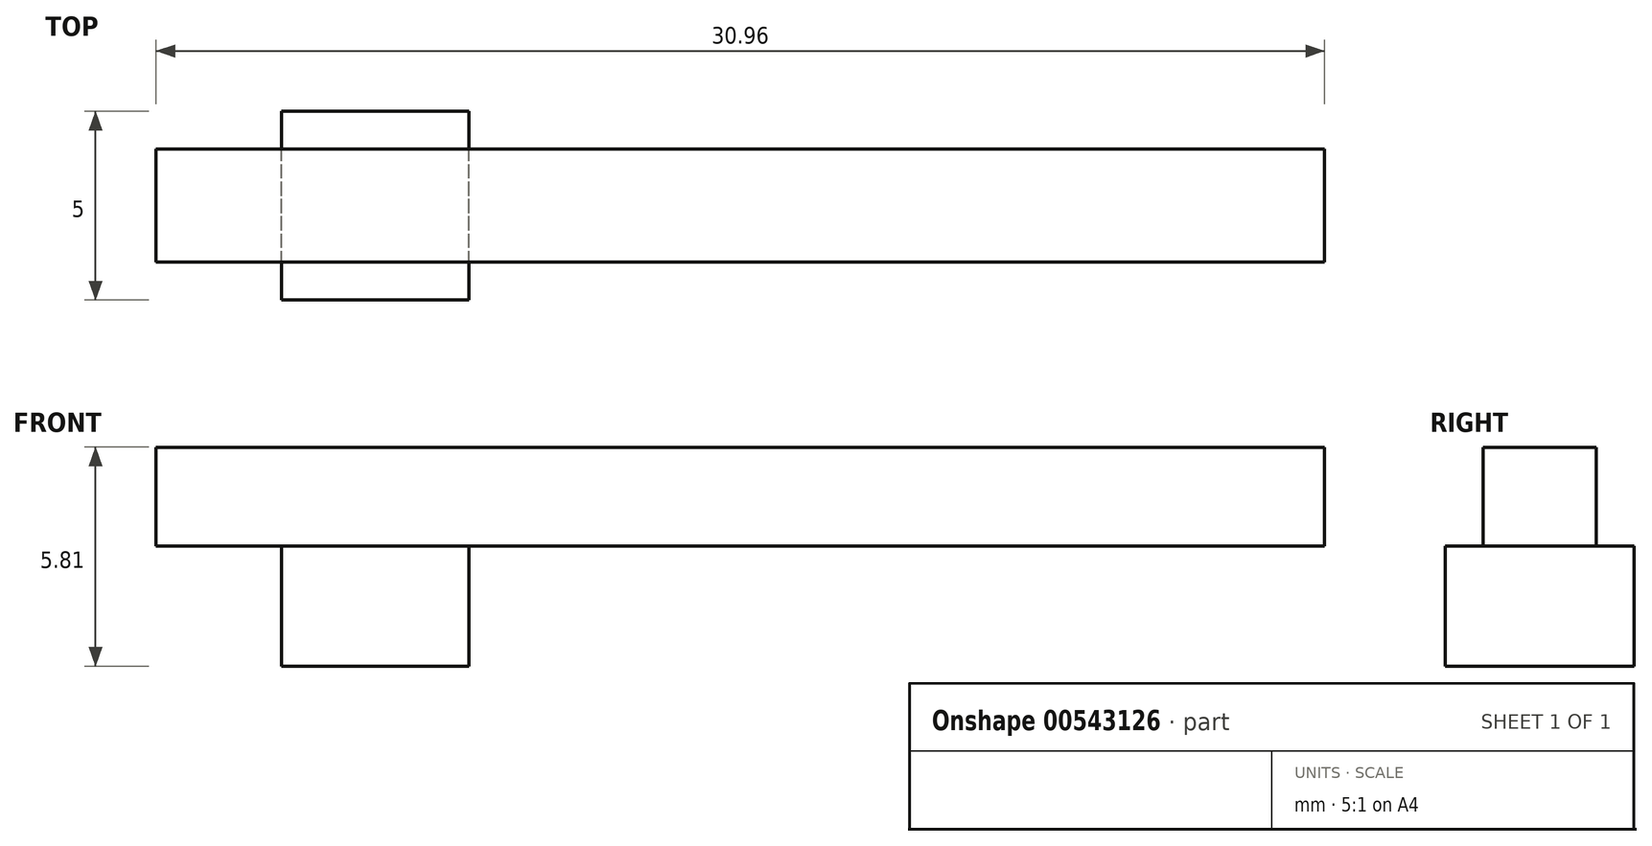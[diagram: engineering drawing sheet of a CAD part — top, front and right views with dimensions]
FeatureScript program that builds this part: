
annotation { "Feature Type Name" : "Feature", "Feature Type Description" : "" }
export const myFeature = defineFeature(function(context is Context, id is Id, definition is map)
    precondition{}
    {
        {
            var Q0;
            Q0=qCreatedBy(makeId("Front.planeOp"),FACE);
            var sketch = newSketch(context, id + "F0", { "sketchPlane" : qUnion([Q0])});
            skLineSegment(sketch, "E0", {"start": v(-43.67, 0) * mm, "end": v(-48.92, 0) * mm});
            skLineSegment(sketch, "E1", {"start": v(-48.92, 0) * mm, "end": v(-48.92, 2.63) * mm});
            skLineSegment(sketch, "E2", {"start": v(-48.92, 2.63) * mm, "end": v(-17.96, 2.63) * mm});
            skLineSegment(sketch, "E3", {"start": v(-17.96, 2.63) * mm, "end": v(-17.96, 0) * mm});
            skLineSegment(sketch, "E4", {"start": v(-17.96, 0) * mm, "end": v(-48.92, 0) * mm});
            skSolve(sketch);
        }
        {
            var Q0;
            {var subQ0=sQuery(id+"F0.wireOp",EDGE,"E1");Q0=makeQuery(id+"F0.imprint","IMPRINT",FACE,{"disambiguationData":[TD([[makeQuery(id+"F0.imprint","IMPRINT",EDGE,{"derivedFrom":subQ0}),-1.0]])]});}
            extrude(context, id + "F1", {"entities" : qUnion([Q0]), "endBound" : BoundingType.SYMMETRIC, "depth" : 3 * mm, "offsetDistance" : 25.4 * mm});
        }
        {
            var Q0;
            Q0=qCreatedBy(makeId("Front.planeOp"),FACE);
            var sketch = newSketch(context, id + "F2", { "sketchPlane" : qUnion([Q0])});
            skLineSegment(sketch, "E5", {"start": v(-45.6, 0) * mm, "end": v(-45.6, -3.18) * mm});
            skLineSegment(sketch, "E6", {"start": v(-45.6, -3.18) * mm, "end": v(-40.63, -3.18) * mm});
            skLineSegment(sketch, "E7", {"start": v(-40.63, -3.18) * mm, "end": v(-40.63, 0) * mm});
            skLineSegment(sketch, "E8", {"start": v(-45.6, 0) * mm, "end": v(-40.63, 0) * mm});
            skSolve(sketch);
        }
        {
            var Q0;
            Q0=makeQuery(id+"F2.imprint","IMPRINT",FACE,{"disambiguationData":[TD([[makeQuery(id+"F2.imprint","IMPRINT",EDGE,{"derivedFrom":sQuery(id+"F2.wireOp",EDGE,"E5")}),1.0]])]});
            extrude(context, id + "F3", {"entities" : qUnion([Q0]), "operationType" : NewBodyOperationType.ADD, "endBound" : BoundingType.SYMMETRIC, "depth" : 5 * mm, "offsetDistance" : 25.4 * mm});
        }
    });
